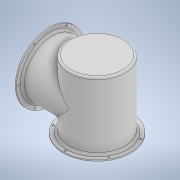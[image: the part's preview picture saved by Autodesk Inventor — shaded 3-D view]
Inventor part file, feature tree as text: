
AUTODESK INVENTOR PART (.ipt)
format: ipt  version: 2021 (Build 250183000, 183)  size: 316,928 bytes
history: native  units: mm
features: sketch x9, extrude x8, revolve x3, hole x3, plane x2, projected_geometry x2, fillet x1
ambient origin geometry x8: Origin, YZ Plane, XZ Plane, XY Plane, X Axis, Y Axis, Z Axis, Center Point
bodies: Solid1 (feature_tree)
feature tree (28):
  revolve  "Revolution1"  [1 undecoded]
  hole  "Hole1"  [1 undecoded]
  fillet  "Fillet1"  [1 undecoded]
  plane  "Work Plane1"
  sketch  "Sketch6"  dims[d10=16.0mm d11=3.0mm]
  extrude  "Extrusion3"  Depth=3.0mm
  extrude  "Extrusion5"  Depth=8.0mm
  extrude  "Extrusion4"  Depth=10.0mm
  revolve  "Revolution2"  [1 undecoded]
  extrude  "Extrusion6"  Depth=165.0mm
  hole  "Hole2"  [1 undecoded]
  extrude  "Extrusion7"  Depth=3.0mm TaperAngle=0.0deg
  plane  "Work Plane2"
  sketch  "Sketch12"  dims[d22=4.5mm d23=10.0mm d24=9.4mm d25=2.0mm d26=90.0deg d27=13.0mm d28=20.594885mm d29=4.5mm]
  extrude  "Extrusion9"  Depth=3.0mm TaperAngle=0.0deg
  extrude  "Extrusion10"  Depth=67.5mm
  extrude  "Extrusion11"  TaperAngle=90.0deg  [1 undecoded]
  revolve  "Revolution3"  [1 undecoded]
  hole  "Hole3"  [1 undecoded]
  sketch  "Sketch2"  dims[d3=90.0deg d5=81.5mm]
  projected_geometry  "Projected Loop1"
  sketch  "Sketch5"  dims[d7=9.0mm d8=5.0mm d9=45.0deg]
  projected_geometry  "Projected Loop6"
  sketch  "Sketch9"  dims[d16=4.5mm d17=8.0mm]
  sketch  "Sketch11"  dims[d18=60.0mm d20=360.0deg]
  sketch  "Sketch14"  dims[d32=2.0mm d33=5.0mm]
  sketch  "Sketch15"  dims[d34=165.0mm d43=9.0mm]
  sketch  "Sketch16"  dims[d50=135.0mm d51=10.0mm d52=0.0mm d53=112.0mm d54=0.0mm d56=48.0mm d57=0.0mm d59=67.5mm d60=90.0deg d62=5.0mm d63=45.0deg d65=48.0mm d66=0.0mm d67=48.0mm d68=0.0mm d74=2.0mm d75=3.0mm d76=67.5mm d78=2.0mm d79=4.5mm d80=4.5mm d81=60.0mm d83=360.0deg d85=4.5mm d86=6.0mm d87=6.3mm d88=2.0mm d89=90.0deg d90=8.0mm d91=20.594885mm d92=75.0mm d93=135.0mm d95=72.0mm d96=10.0mm d97=0.0mm d98=35.0mm d99=0.0mm d100=2.0mm d101=48.0mm d102=0.0mm d103=9.0mm d105=5.0mm d106=45.0deg d107=3.0mm d109=67.5mm d110=67.5mm d111=90.0deg d112=4.5mm d113=4.5mm d114=60.0mm d116=360.0deg d118=4.5mm d119=6.0mm d120=9.4mm d121=2.0mm d122=90.0deg d123=8.0mm d124=20.594885mm d125=3.0mm]
note: 8 required parameter values undecoded (feature->parameter linkage not recoverable at this tier; creation-order binding heuristic only, values carry confidence <= 0.55)